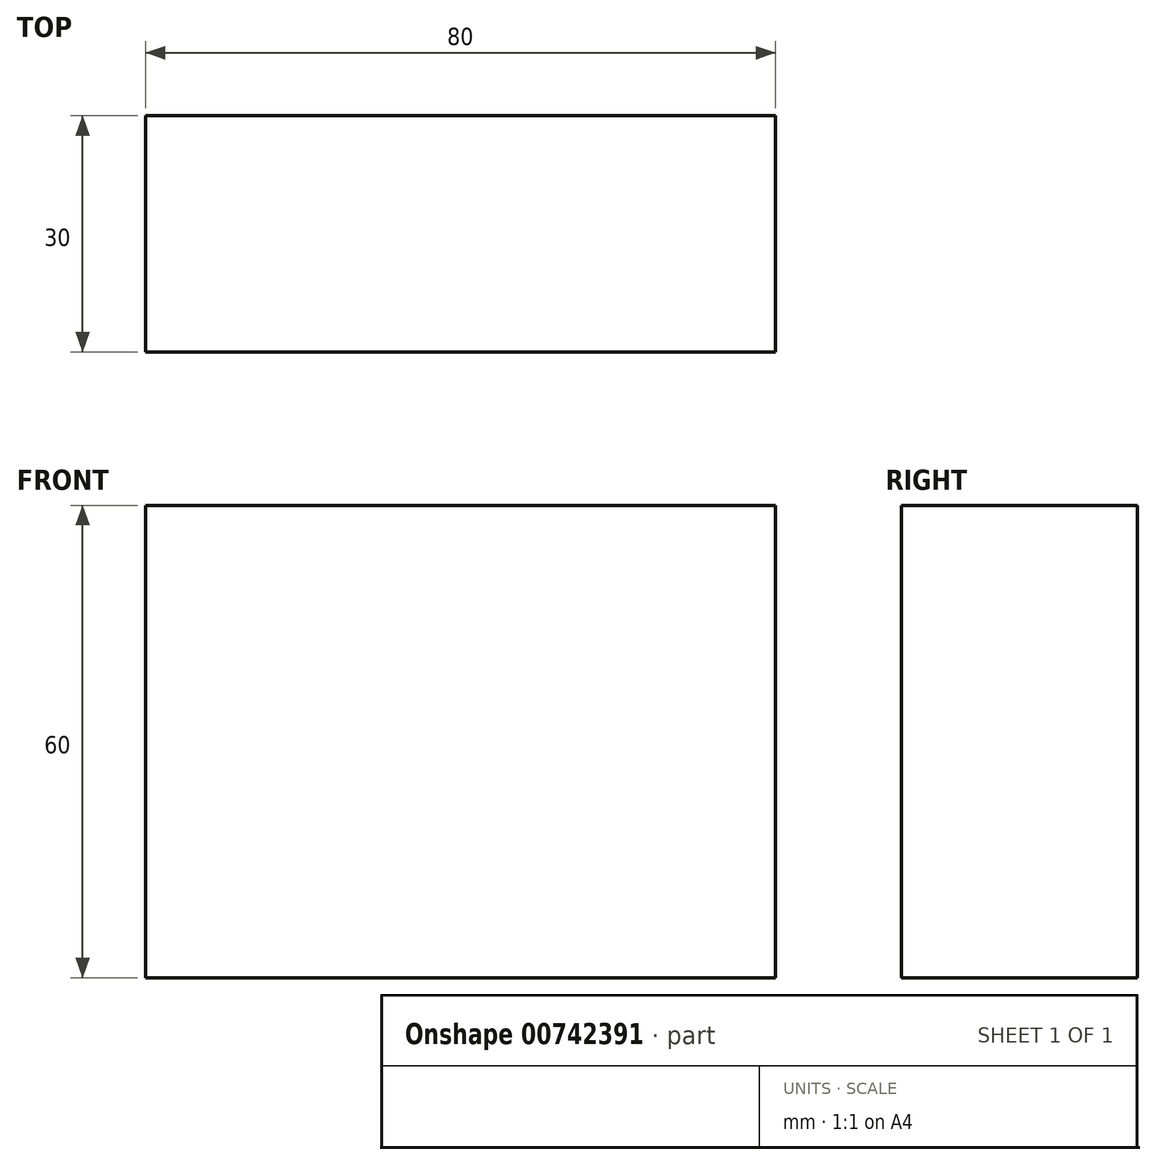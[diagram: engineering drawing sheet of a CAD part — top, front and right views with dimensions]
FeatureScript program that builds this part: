
annotation { "Feature Type Name" : "Feature", "Feature Type Description" : "" }
export const myFeature = defineFeature(function(context is Context, id is Id, definition is map)
    precondition{}
    {
        {
            var Q0;
            Q0=qCreatedBy(makeId("Front.planeOp"),FACE);
            var sketch = newSketch(context, id + "F0", { "sketchPlane" : qUnion([Q0])});
            skLineSegment(sketch, "E0.bottom", {"start": v(-80, 0) * mm, "end": v(0, 0) * mm});
            skLineSegment(sketch, "E0.top", {"start": v(-80, -60) * mm, "end": v(0, -60) * mm});
            skLineSegment(sketch, "E0.left", {"start": v(-80, 0) * mm, "end": v(-80, -60) * mm});
            skLineSegment(sketch, "E0.right", {"start": v(0, 0) * mm, "end": v(0, -60) * mm});
            skLineSegment(sketch, "E1.bottom", {"start": v(-80, 0) * mm, "end": v(-60, 0) * mm});
            skLineSegment(sketch, "E1.top", {"start": v(-80, -60) * mm, "end": v(-21.78, -60) * mm});
            skLineSegment(sketch, "E2.bottom", {"start": v(0, 0) * mm, "end": v(-20, 0) * mm});
            skLineSegment(sketch, "E2.top", {"start": v(0, -60) * mm, "end": v(-20, -60) * mm});
            skLineSegment(sketch, "E3.bottom", {"start": v(-20, 0) * mm, "end": v(0, 0) * mm});
            skLineSegment(sketch, "E3.top", {"start": v(-20, -60) * mm, "end": v(0, -60) * mm});
            skLineSegment(sketch, "E3.left", {"start": v(-20, 0) * mm, "end": v(-20, -60) * mm});
            skLineSegment(sketch, "E4.bottom", {"start": v(-60, 0) * mm, "end": v(-80, 0) * mm});
            skLineSegment(sketch, "E4.top", {"start": v(-60, -60) * mm, "end": v(-80, -60) * mm});
            skLineSegment(sketch, "E4.left", {"start": v(-60, 0) * mm, "end": v(-60, -60) * mm});
            skLineSegment(sketch, "E5.bottom", {"start": v(0, 0) * mm, "end": v(-10, 0) * mm});
            skLineSegment(sketch, "E5.top", {"start": v(0, -60) * mm, "end": v(-10, -60) * mm});
            skLineSegment(sketch, "E5.right", {"start": v(-10, 0) * mm, "end": v(-10, -60) * mm});
            skLineSegment(sketch, "E6.bottom", {"start": v(-70, 0) * mm, "end": v(-80, 0) * mm});
            skLineSegment(sketch, "E6.top", {"start": v(-70, -60) * mm, "end": v(-80, -60) * mm});
            skLineSegment(sketch, "E6.left", {"start": v(-70, 0) * mm, "end": v(-70, -60) * mm});
            skSolve(sketch);
        }
        {
            var Q0;
            Q0 = qSketchRegion(id + "F0", true);
            extrude(context, id + "F1", {"entities" : qUnion([Q0]), "depth" : 40 * mm, "offsetDistance" : 25 * mm});
        }
        {
            var Q0;
            Q0=makeQuery(id+"F1.opExtrude","CAP_FACE",FACE,{"disambiguationData":[OSD([sQuery(id+"F0.wireOp",EDGE,"E0.bottom"),sQuery(id+"F0.wireOp",EDGE,"E0.top"),sQuery(id+"F0.wireOp",EDGE,"E1.bottom"),sQuery(id+"F0.wireOp",EDGE,"E1.top"),sQuery(id+"F0.wireOp",EDGE,"E0.left"),sQuery(id+"F0.wireOp",EDGE,"E2.bottom"),sQuery(id+"F0.wireOp",EDGE,"E2.top"),sQuery(id+"F0.wireOp",EDGE,"E0.right")])],"isStart":false});
            var sketch = newSketch(context, id + "F2", { "sketchPlane" : qUnion([Q0])});
            skLineSegment(sketch, "E7.bottom", {"start": v(-80, 0) * mm, "end": v(-60, 0) * mm});
            skLineSegment(sketch, "E7.top", {"start": v(-80, -60) * mm, "end": v(-60, -60) * mm});
            skLineSegment(sketch, "E7.left", {"start": v(-80, 0) * mm, "end": v(-80, -60) * mm});
            skLineSegment(sketch, "E7.right", {"start": v(-60, 0) * mm, "end": v(-60, -60) * mm});
            skLineSegment(sketch, "E8.bottom", {"start": v(0, 0) * mm, "end": v(-20, 0) * mm});
            skLineSegment(sketch, "E8.top", {"start": v(0, -60) * mm, "end": v(-20, -60) * mm});
            skLineSegment(sketch, "E8.left", {"start": v(0, 0) * mm, "end": v(0, -60) * mm});
            skLineSegment(sketch, "E8.right", {"start": v(-20, 0) * mm, "end": v(-20, -60) * mm});
            skSolve(sketch);
        }
        {
            var Q0;
            Q0 = qSketchRegion(id + "F0", true);
            var Q1;
            Q1=makeQuery(id+"F2.imprint","IMPRINT",FACE,{"disambiguationData":[TD([[makeQuery(id+"F2.imprint","IMPRINT",EDGE,{"derivedFrom":sQuery(id+"F2.wireOp",EDGE,"E7.bottom")}),1.0]])]});
            var Q2;
            Q2=makeQuery(id+"F2.imprint","IMPRINT",FACE,{"disambiguationData":[TD([[makeQuery(id+"F2.imprint","IMPRINT",EDGE,{"derivedFrom":sQuery(id+"F2.wireOp",EDGE,"E8.bottom")}),1.0]])]});
            extrude(context, id + "F3", {"entities" : qUnion([Q0, Q1, Q2]), "operationType" : NewBodyOperationType.REMOVE, "oppositeDirection" : true, "depth" : 20 * mm, "offsetDistance" : 25 * mm});
        }
        {
            var Q0;
            Q0=makeQuery(id+"F0.imprint","IMPRINT",FACE,{"disambiguationData":[TD([[makeQuery(id+"F0.imprint","IMPRINT",EDGE,{"derivedFrom":sQuery(id+"F0.wireOp",EDGE,"E4.bottom")}),1.0]])]});
            var Q1;
            Q1=makeQuery(id+"F0.imprint","IMPRINT",FACE,{"disambiguationData":[TD([[makeQuery(id+"F0.imprint","IMPRINT",EDGE,{"derivedFrom":sQuery(id+"F0.wireOp",EDGE,"E0.bottom")}),-1.0]])]});
            var Q2;
            Q2=makeQuery(id+"F0.imprint","IMPRINT",FACE,{"disambiguationData":[TD([[makeQuery(id+"F0.imprint","IMPRINT",EDGE,{"derivedFrom":sQuery(id+"F0.wireOp",EDGE,"E3.bottom")}),-1.0]])]});
            extrude(context, id + "F4", {"entities" : qUnion([Q0, Q1, Q2]), "operationType" : NewBodyOperationType.REMOVE, "depth" : 10 * mm, "offsetDistance" : 25 * mm});
        }
    });
